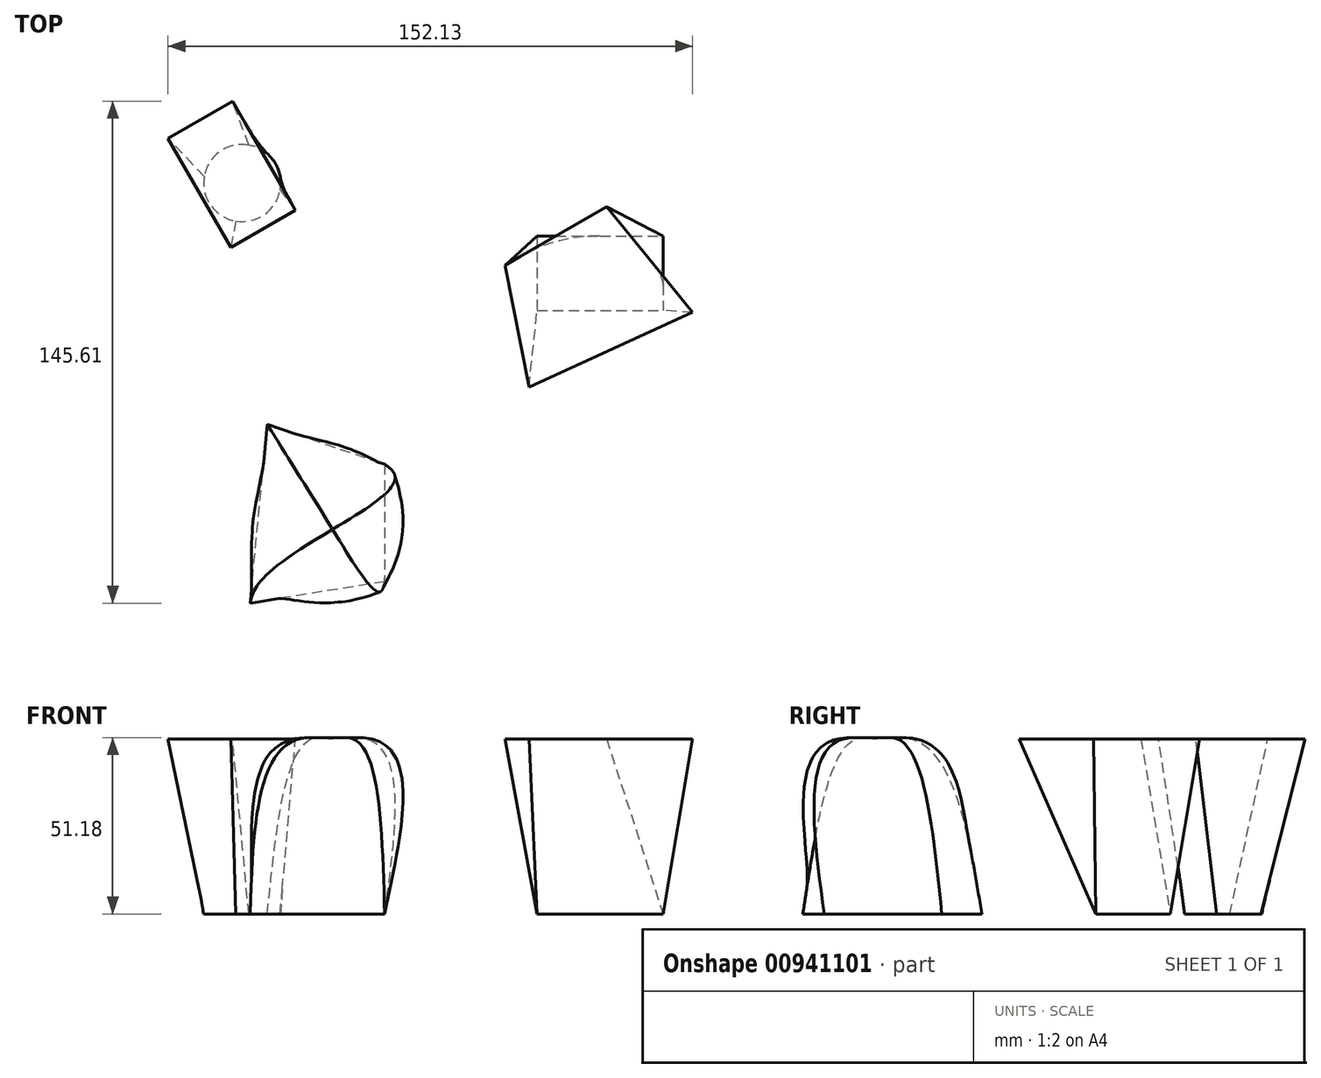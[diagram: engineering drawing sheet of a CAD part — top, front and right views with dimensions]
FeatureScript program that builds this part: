
annotation { "Feature Type Name" : "Feature", "Feature Type Description" : "" }
export const myFeature = defineFeature(function(context is Context, id is Id, definition is map)
    precondition{}
    {
        {
            var Q0;
            Q0=qCreatedBy(makeId("Top.planeOp"),FACE);
            var sketch = newSketch(context, id + "F0", { "sketchPlane" : qUnion([Q0])});
            skCircle(sketch, "E0", {"center": v(-62.28, 52.52) * mm, "radius": 11.18 * mm});
            skLineSegment(sketch, "E1.bottom", {"start": v(23.25, 37.16) * mm, "end": v(59.79, 37.16) * mm});
            skLineSegment(sketch, "E1.top", {"start": v(23.25, 15.57) * mm, "end": v(59.79, 15.57) * mm});
            skLineSegment(sketch, "E1.left", {"start": v(23.25, 37.16) * mm, "end": v(23.25, 15.57) * mm});
            skLineSegment(sketch, "E1.right", {"start": v(59.79, 37.16) * mm, "end": v(59.79, 15.57) * mm});
            skLineSegment(sketch, "E2", {"start": v(-55, -17.45) * mm, "end": v(-20.95, -29.08) * mm});
            skLineSegment(sketch, "E3", {"start": v(-20.95, -29.08) * mm, "end": v(-20.95, -63.13) * mm});
            skLineSegment(sketch, "E4", {"start": v(-20.95, -63.13) * mm, "end": v(-59.98, -69.35) * mm});
            skLineSegment(sketch, "E5", {"start": v(-59.98, -69.35) * mm, "end": v(-55, -17.45) * mm});
            skLineSegment(sketch, "E6", {"start": v(-82.91, 71.7) * mm, "end": v(-82.91, 30.26) * mm, "construction": true});
            skSolve(sketch);
        }
        {
            var Q0;
            Q0=qCreatedBy(makeId("Top.planeOp"),FACE);
            cPlane(context, id + "F1", {"entities" : qUnion([Q0]), "cplaneType" : CPlaneType.OFFSET, "offset" : 50.8 * mm, "width" : 152.4 * mm, "height" : 152.4 * mm});
        }
        {
            var Q0;
            Q0=qCreatedBy(id+"F1.planeOp",FACE);
            var sketch = newSketch(context, id + "F2", { "sketchPlane" : qUnion([Q0])});
            skCircle(sketch, "E7.0", {"center": v(-36.07, -47.94) * mm, "radius": 11.18 * mm});
            skLineSegment(sketch, "E7.1.0", {"start": v(-65.53, 33.82) * mm, "end": v(-46.83, 44.61) * mm});
            skLineSegment(sketch, "E7.1.1", {"start": v(-46.83, 44.61) * mm, "end": v(-65.1, 76.26) * mm});
            skLineSegment(sketch, "E7.1.2", {"start": v(-65.1, 76.26) * mm, "end": v(-83.8, 65.46) * mm});
            skLineSegment(sketch, "E7.1.3", {"start": v(-83.8, 65.46) * mm, "end": v(-65.53, 33.82) * mm});
            skLineSegment(sketch, "E7.2.0", {"start": v(20.9, -6.64) * mm, "end": v(68.33, 15) * mm});
            skLineSegment(sketch, "E7.2.1", {"start": v(68.33, 15) * mm, "end": v(43.42, 45.68) * mm});
            skLineSegment(sketch, "E7.2.2", {"start": v(43.42, 45.68) * mm, "end": v(13.94, 28.66) * mm});
            skLineSegment(sketch, "E7.2.3", {"start": v(13.94, 28.66) * mm, "end": v(20.9, -6.64) * mm});
            skSolve(sketch);
        }
        {
            var Q0;
            Q0=makeQuery(id+"F2.imprint","IMPRINT",FACE,{"disambiguationData":[TD([[makeQuery(id+"F2.imprint","IMPRINT",EDGE,{"derivedFrom":sQuery(id+"F2.wireOp",EDGE,"E7.2.0")}),1.0]])]});
            var Q1;
            Q1=makeQuery(id+"F0.imprint","IMPRINT",FACE,{"disambiguationData":[TD([[makeQuery(id+"F0.imprint","IMPRINT",EDGE,{"derivedFrom":sQuery(id+"F0.wireOp",EDGE,"E1.bottom")}),-1.0]])]});
            loft(context, id + "F3", {"sheetProfilesArray" : [{ "sheetProfileEntities" : qUnion([Q0]) }, { "sheetProfileEntities" : qUnion([Q1]) }]});
        }
        {
            var Q0;
            Q0=makeQuery(id+"F0.imprint","IMPRINT",FACE,{"disambiguationData":[TD([[makeQuery(id+"F0.imprint","IMPRINT",EDGE,{"derivedFrom":sQuery(id+"F0.wireOp",EDGE,"E0")}),1.0]])]});
            var Q1;
            Q1=makeQuery(id+"F2.imprint","IMPRINT",FACE,{"disambiguationData":[TD([[makeQuery(id+"F2.imprint","IMPRINT",EDGE,{"derivedFrom":sQuery(id+"F2.wireOp",EDGE,"E7.1.0")}),1.0]])]});
            loft(context, id + "F4", {"sheetProfilesArray" : [{ "sheetProfileEntities" : qUnion([Q0]) }, { "sheetProfileEntities" : qUnion([Q1]) }]});
        }
        {
            var Q0;
            Q0=makeQuery(id+"F0.imprint","IMPRINT",FACE,{"disambiguationData":[TD([[makeQuery(id+"F0.imprint","IMPRINT",EDGE,{"derivedFrom":sQuery(id+"F0.wireOp",EDGE,"E2")}),-1.0]])]});
            var Q1;
            Q1=makeQuery(id+"F2.imprint","IMPRINT",FACE,{"disambiguationData":[TD([[makeQuery(id+"F2.imprint","IMPRINT",EDGE,{"derivedFrom":sQuery(id+"F2.wireOp",EDGE,"E7.0")}),1.0]])]});
            var Q2;
            Q2=sQuery(id+"F2.wireOp",VERTEX,"E7.0.center");
            loft(context, id + "F5", {"sheetProfilesArray" : [{ "sheetProfileEntities" : qUnion([Q0]) }, { "sheetProfileEntities" : qUnion([Q1]) }, { "sheetProfileEntities" : qUnion([Q2]) }]});
        }
    });
